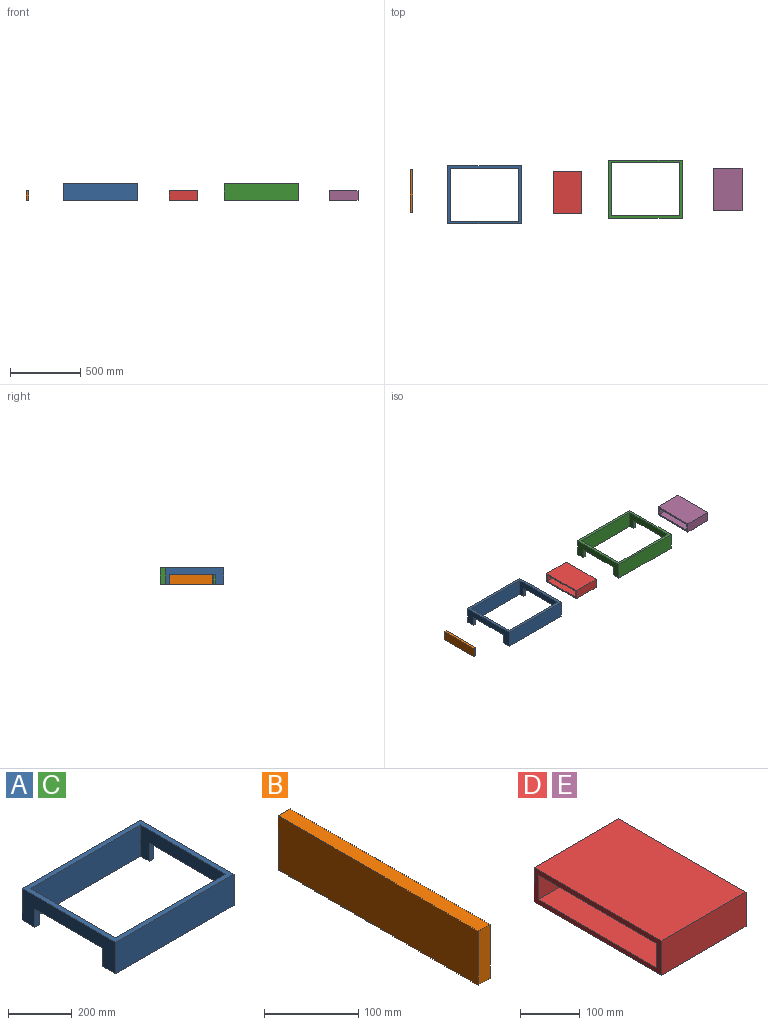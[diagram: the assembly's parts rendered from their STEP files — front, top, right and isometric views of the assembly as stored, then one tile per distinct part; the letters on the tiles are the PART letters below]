
ASSEMBLY  parts=5 mates=4
PART A: 17 faces, bbox 525x415x120 mm
  f0: plane 415x120mm, normal (1,0,0), area 28800mm2, adj f1,f6,f7,f9,f10,f11,f12,f13
  f1: plane 525x57.5mm, normal (0,0,-1), area 10872mm2, adj f0,f3,f4,f5,f7,f8,f13,f15
  f2: plane 489x120mm, normal (0,1,0), area 58680mm2, adj f3,f8,f9,f10
  f3: plane 379x120mm, normal (1,0,0), area 24480mm2, adj f1,f2,f4,f9,f10,f14,f15,f16
  f4: plane 489x120mm, normal (0,-1,0), area 58680mm2, adj f1,f3,f8,f9
  f5: plane 415x120mm, normal (-1,0,0), area 28800mm2, adj f1,f6,f7,f9,f10,f14,f15,f16
  f6: plane 525x120mm, normal (0,-1,0), area 63000mm2, adj f0,f5,f9,f10
  f7: plane 525x120mm, normal (0,1,0), area 63000mm2, adj f0,f1,f5,f9
  f8: plane 379x120mm, normal (-1,0,0), area 24480mm2, adj f1,f2,f4,f9,f10,f11,f12,f13
  f9: plane 525x415mm, normal (0,0,1), area 32544mm2, adj f0,f2,f3,f4,f5,f6,f7,f8
  f10: plane 525x57.5mm, normal (0,0,-1), area 10872mm2, adj f0,f2,f3,f5,f6,f8,f11,f16
  f11: plane 70x18mm, normal (0,1,0), area 1260mm2, adj f0,f8,f10,f12
  f12: plane 300x18mm, normal (0,0,-1), area 5400mm2, adj f0,f8,f11,f13
  f13: plane 70x18mm, normal (0,-1,0), area 1260mm2, adj f0,f1,f8,f12
  f14: plane 300x18mm, normal (0,0,-1), area 5400mm2, adj f3,f5,f15,f16
  f15: plane 70x18mm, normal (0,-1,0), area 1260mm2, adj f1,f3,f5,f14
  f16: plane 70x18mm, normal (0,1,0), area 1260mm2, adj f3,f5,f10,f14
PART B: 6 faces, bbox 18x300x70 mm
  f0: plane 70x18mm, normal (0,-1,0), area 1260mm2, adj f1,f3,f4,f5
  f1: plane 300x18mm, normal (0,0,-1), area 5400mm2, adj f0,f2,f4,f5
  f2: plane 70x18mm, normal (0,1,0), area 1260mm2, adj f1,f3,f4,f5
  f3: plane 300x18mm, normal (0,0,1), area 5400mm2, adj f0,f2,f4,f5
  f4: plane 300x70mm, normal (1,0,0), area 21000mm2, adj f0,f1,f2,f3
  f5: plane 300x70mm, normal (-1,0,0), area 21000mm2, adj f0,f1,f2,f3
PART C: same geometry as A
PART D: 10 faces, bbox 200x300x70 mm
  f0: plane 200x50mm, normal (0,1,0), area 10000mm2, adj f1,f7,f8,f9
  f1: plane 280x200mm, normal (0,0,-1), area 56000mm2, adj f0,f2,f8,f9
  f2: plane 200x50mm, normal (0,-1,0), area 10000mm2, adj f1,f7,f8,f9
  f3: plane 200x70mm, normal (0,-1,0), area 14000mm2, adj f4,f6,f8,f9
  f4: plane 300x200mm, normal (0,0,-1), area 60000mm2, adj f3,f5,f8,f9
  f5: plane 200x70mm, normal (0,1,0), area 14000mm2, adj f4,f6,f8,f9
  f6: plane 300x200mm, normal (0,0,1), area 60000mm2, adj f3,f5,f8,f9
  f7: plane 280x200mm, normal (0,0,1), area 56000mm2, adj f0,f2,f8,f9
  f8: plane 300x70mm, normal (1,0,0), area 7000mm2, adj f0,f1,f2,f3,f4,f5,f6,f7
  f9: plane 300x70mm, normal (-1,0,0), area 7000mm2, adj f0,f1,f2,f3,f4,f5,f6,f7
PART E: same geometry as D
PLACE A t=(-759.24,-261.53,-771.21)mm
PLACE B t=(-1027.36,-177.6,-771.21)mm
PLACE C t=(384.99,-223.08,-771.21)mm
PLACE D t=(-8.29,-187.78,-771.21)mm
PLACE E t=(1135.14,-167.12,-771.21)mm
MATE planar C.f1 <-> D.f4  axis (0,0,-1) through (647.49,179.16,-771.21)mm
MATE planar A.f1 <-> D.f4  axis (0,0,-1) through (-234.24,124.72,-771.21)mm
MATE planar C.f1 <-> E.f4  axis (0,0,-1) through (647.49,179.16,-771.21)mm
MATE planar A.f1 <-> B.f1  axis (0,0,-1) through (-741.24,135.47,-771.21)mm
